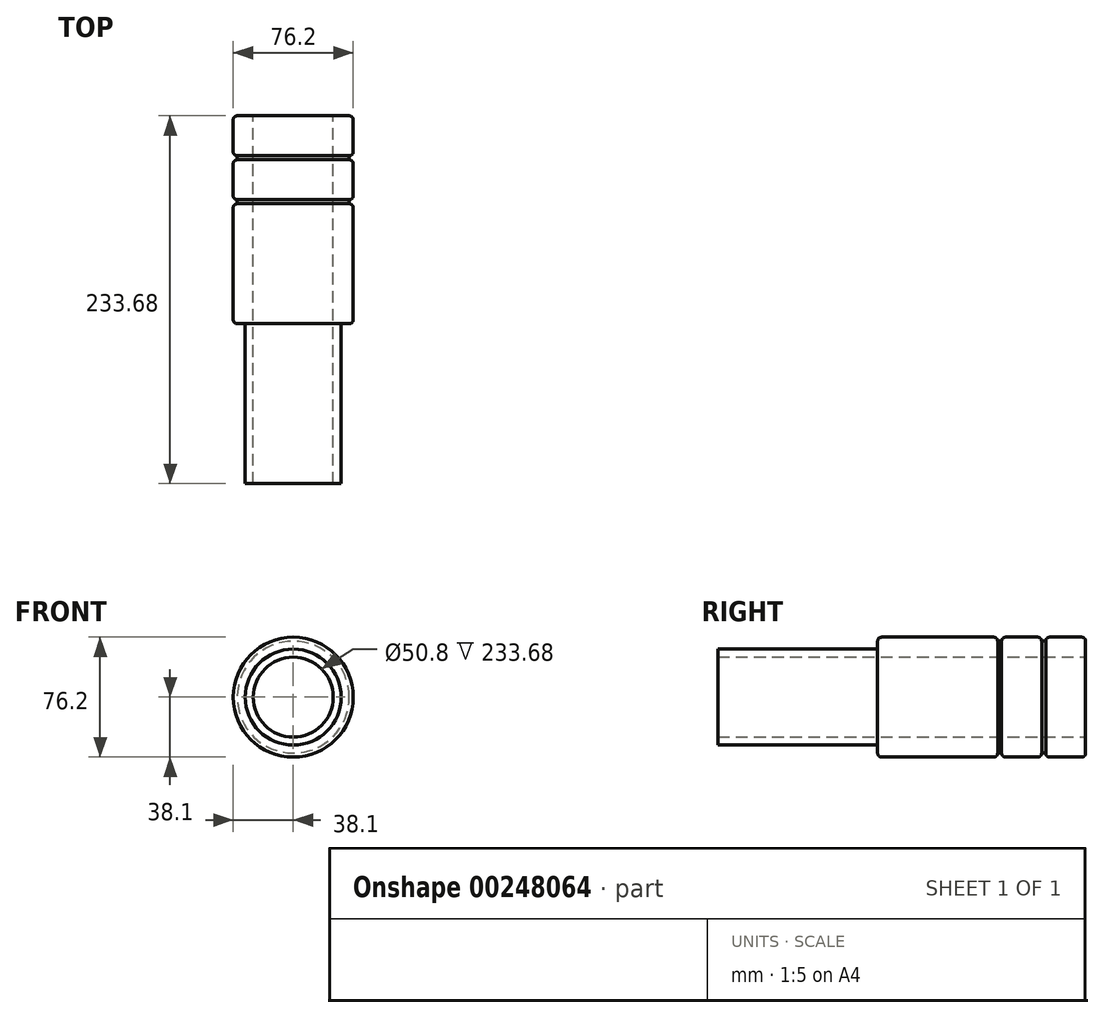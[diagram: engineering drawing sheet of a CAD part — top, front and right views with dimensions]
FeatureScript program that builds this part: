
annotation { "Feature Type Name" : "Feature", "Feature Type Description" : "" }
export const myFeature = defineFeature(function(context is Context, id is Id, definition is map)
    precondition{}
    {
        {
            var Q0;
            Q0=qCreatedBy(makeId("Front.planeOp"),FACE);
            var sketch = newSketch(context, id + "F0", { "sketchPlane" : qUnion([Q0])});
            skCircle(sketch, "E0", {"center": v(0, 0) * mm, "radius": 38.1 * mm});
            skSolve(sketch);
        }
        {
            var Q0;
            Q0 = qSketchRegion(id + "F0", true);
            extrude(context, id + "F1", {"entities" : qUnion([Q0]), "oppositeDirection" : true, "depth" : 25.4 * mm});
        }
        {
            var Q0;
            Q0=makeQuery(id+"F1.opExtrude","CAP_FACE",FACE,{"disambiguationData":[OSD([sQuery(id+"F0.wireOp",EDGE,"E0")])],"isStart":false});
            var sketch = newSketch(context, id + "F2", { "sketchPlane" : qUnion([Q0])});
            skCircle(sketch, "E1", {"center": v(0, 0) * mm, "radius": 25.4 * mm});
            skSolve(sketch);
        }
        {
            var Q0;
            Q0=makeQuery(id+"F2.imprint","IMPRINT",FACE,{"disambiguationData":[TD([[makeQuery(id+"F2.imprint","IMPRINT",EDGE,{"derivedFrom":sQuery(id+"F2.wireOp",EDGE,"E1")}),1.0]])]});
            extrude(context, id + "F3", {"entities" : qUnion([Q0]), "operationType" : NewBodyOperationType.REMOVE, "endBound" : BoundingType.THROUGH_ALL, "oppositeDirection" : true, "depth" : 25.4 * mm});
        }
        {
            var Q0;
            Q0=makeQuery(id+"F1.opExtrude","CAP_FACE",FACE,{"disambiguationData":[OSD([sQuery(id+"F0.wireOp",EDGE,"E0")])],"isStart":true});
            var sketch = newSketch(context, id + "F4", { "sketchPlane" : qUnion([Q0])});
            skCircle(sketch, "E2", {"center": v(0, 0) * mm, "radius": 25.4 * mm});
            skCircle(sketch, "E3", {"center": v(0, 0) * mm, "radius": 35.56 * mm});
            skSolve(sketch);
        }
        {
            var Q0;
            Q0=makeQuery(id+"F4.imprint","IMPRINT",FACE,{"disambiguationData":[TD([[makeQuery(id+"F4.imprint","IMPRINT",EDGE,{"derivedFrom":sQuery(id+"F4.wireOp",EDGE,"E2")}),-1.0]])]});
            extrude(context, id + "F5", {"entities" : qUnion([Q0]), "operationType" : NewBodyOperationType.ADD, "depth" : 2.54 * mm});
        }
        {
            var Q0;
            Q0=makeQuery(id+"F1.opExtrude","SWEPT_FACE",FACE,{"disambiguationData":[OSD([sQuery(id+"F0.wireOp",EDGE,"E0")])]});
            fillet(context, id + "F6", {"entities" : qUnion([Q0]), "radius" : 2.54 * mm, "tangentPropagation" : true, "allowEdgeOverflow" : false});
        }
        {
            var Q0;
            Q0=makeQuery(id+"F5.opExtrude","CAP_FACE",FACE,{"disambiguationData":[OSD([sQuery(id+"F4.wireOp",EDGE,"E2"),sQuery(id+"F4.wireOp",EDGE,"E3")])],"isStart":false});
            var sketch = newSketch(context, id + "F7", { "sketchPlane" : qUnion([Q0])});
            skCircle(sketch, "E4", {"center": v(0, 0) * mm, "radius": 38.1 * mm});
            skCircle(sketch, "E5", {"center": v(0, 0) * mm, "radius": 25.4 * mm});
            skSolve(sketch);
        }
        {
            var Q0;
            Q0=makeQuery(id+"F7.imprint","IMPRINT",FACE,{"disambiguationData":[TD([[makeQuery(id+"F7.imprint","IMPRINT",EDGE,{"derivedFrom":sQuery(id+"F7.wireOp",EDGE,"E4")}),1.0]])]});
            var Q1;
            Q1=makeQuery(id+"F7.imprint","IMPRINT",FACE,{"disambiguationData":[TD([[makeQuery(id+"F7.imprint","IMPRINT",EDGE,{"derivedFrom":sQuery(id+"F7.wireOp",EDGE,"E5")}),-1.0]])]});
            extrude(context, id + "F8", {"entities" : qUnion([Q0, Q1]), "operationType" : NewBodyOperationType.ADD, "depth" : 25.4 * mm});
        }
        {
            var Q0;
            Q0=makeQuery(id+"F8.opExtrude","CAP_EDGE",EDGE,{"disambiguationData":[OSD([sQuery(id+"F7.wireOp",EDGE,"E4")])],"isStart":true});
            fillet(context, id + "F9", {"entities" : qUnion([Q0]), "radius" : 2.54 * mm, "tangentPropagation" : true, "allowEdgeOverflow" : false});
        }
        {
            var Q0;
            Q0=makeQuery(id+"F8.opExtrude","CAP_EDGE",EDGE,{"disambiguationData":[OSD([sQuery(id+"F7.wireOp",EDGE,"E4")])],"isStart":false});
            fillet(context, id + "F10", {"entities" : qUnion([Q0]), "radius" : 2.54 * mm, "tangentPropagation" : true, "allowEdgeOverflow" : false});
        }
        {
            var Q0;
            Q0=makeQuery(id+"F8.opExtrude","CAP_FACE",FACE,{"disambiguationData":[OSD([sQuery(id+"F7.wireOp",EDGE,"E4"),sQuery(id+"F7.wireOp",EDGE,"E5")])],"isStart":false});
            var sketch = newSketch(context, id + "F11", { "sketchPlane" : qUnion([Q0])});
            skCircle(sketch, "E6", {"center": v(0, 0) * mm, "radius": 25.4 * mm});
            skCircle(sketch, "E7", {"center": v(0, 0) * mm, "radius": 35.56 * mm});
            skSolve(sketch);
        }
        {
            var Q0;
            Q0=makeQuery(id+"F11.imprint","IMPRINT",FACE,{"disambiguationData":[TD([[makeQuery(id+"F11.imprint","IMPRINT",EDGE,{"derivedFrom":sQuery(id+"F11.wireOp",EDGE,"E6")}),-1.0]])]});
            var sketch = newSketch(context, id + "F12", { "sketchPlane" : qUnion([Q0])});
            skSolve(sketch);
        }
        {
            var Q0;
            Q0 = qSketchRegion(id + "F12", true);
            var Q1;
            Q1=makeQuery(id+"F11.imprint","IMPRINT",FACE,{"disambiguationData":[TD([[makeQuery(id+"F11.imprint","IMPRINT",EDGE,{"derivedFrom":sQuery(id+"F11.wireOp",EDGE,"E6")}),-1.0]])]});
            extrude(context, id + "F13", {"entities" : qUnion([Q0, Q1]), "operationType" : NewBodyOperationType.ADD, "depth" : 2.54 * mm});
        }
        {
            var Q0;
            Q0=makeQuery(id+"F13.opExtrude","CAP_FACE",FACE,{"disambiguationData":[OSD([sQuery(id+"F11.wireOp",EDGE,"E6"),sQuery(id+"F11.wireOp",EDGE,"E7")])],"isStart":false});
            var sketch = newSketch(context, id + "F14", { "sketchPlane" : qUnion([Q0])});
            skCircle(sketch, "E8", {"center": v(0, 0) * mm, "radius": 25.4 * mm});
            skCircle(sketch, "E9", {"center": v(0, 0) * mm, "radius": 38.1 * mm});
            skSolve(sketch);
        }
        {
            var Q0;
            Q0=makeQuery(id+"F14.imprint","IMPRINT",FACE,{"disambiguationData":[TD([[makeQuery(id+"F14.imprint","IMPRINT",EDGE,{"derivedFrom":sQuery(id+"F14.wireOp",EDGE,"E9")}),1.0]])]});
            var Q1;
            Q1=makeQuery(id+"F14.imprint","IMPRINT",FACE,{"disambiguationData":[TD([[makeQuery(id+"F14.imprint","IMPRINT",EDGE,{"derivedFrom":sQuery(id+"F14.wireOp",EDGE,"E8")}),-1.0]])]});
            var Q2;
            Q2=sQuery(id+"F14.wireOp",EDGE,"E9");
            extrude(context, id + "F15", {"entities" : qUnion([Q0, Q1]), "operationType" : NewBodyOperationType.ADD, "surfaceEntities" : qUnion([Q2]), "depth" : 76.2 * mm});
        }
        {
            var Q0;
            Q0=makeQuery(id+"F15.opExtrude","CAP_EDGE",EDGE,{"disambiguationData":[OSD([sQuery(id+"F14.wireOp",EDGE,"E9")])],"isStart":true});
            var Q1;
            Q1=makeQuery(id+"F15.opExtrude","CAP_EDGE",EDGE,{"disambiguationData":[OSD([sQuery(id+"F14.wireOp",EDGE,"E9")])],"isStart":false});
            fillet(context, id + "F16", {"entities" : qUnion([Q0, Q1]), "radius" : 2.54 * mm, "tangentPropagation" : true, "allowEdgeOverflow" : false});
        }
        {
            var Q0;
            Q0=makeQuery(id+"F15.opExtrude","CAP_FACE",FACE,{"disambiguationData":[OSD([sQuery(id+"F14.wireOp",EDGE,"E8"),sQuery(id+"F14.wireOp",EDGE,"E9")])],"isStart":false});
            var sketch = newSketch(context, id + "F17", { "sketchPlane" : qUnion([Q0])});
            skCircle(sketch, "E10", {"center": v(0, 0) * mm, "radius": 25.4 * mm});
            skCircle(sketch, "E11", {"center": v(0, 0) * mm, "radius": 30.48 * mm});
            skSolve(sketch);
        }
        {
            var Q0;
            Q0=makeQuery(id+"F17.imprint","IMPRINT",FACE,{"disambiguationData":[TD([[makeQuery(id+"F17.imprint","IMPRINT",EDGE,{"derivedFrom":sQuery(id+"F17.wireOp",EDGE,"E10")}),-1.0]])]});
            extrude(context, id + "F18", {"entities" : qUnion([Q0]), "operationType" : NewBodyOperationType.ADD, "depth" : 101.6 * mm});
        }
    });
